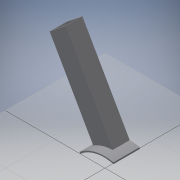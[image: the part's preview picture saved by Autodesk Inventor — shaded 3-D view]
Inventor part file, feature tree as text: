
AUTODESK INVENTOR PART (.ipt)
format: ipt  version: 2019 (Build 230136000, 136)  size: 164,352 bytes
history: native  units: mm
features: other x5, extrude x4, sketch x4, reference x4, projected_geometry x2
ambient origin geometry x8: Origin, YZ Plane, XZ Plane, XY Plane, X Axis, Y Axis, Z Axis, Center Point
bodies: Body1 (feature_tree)
feature tree (19):
  other  "Твердое тело1"
  extrude  "Выдавливание1"  Depth=3.0mm
  extrude  "Выдавливание2"  Depth=3.0mm
  extrude  "Выдавливание3"  Depth=19.0mm TaperAngle=0.0deg
  extrude  "Выдавливание4"  TaperAngle=180.0deg  [1 undecoded]
  sketch  "Эскиз1"
  reference  "Ссылка1"
  reference  "Ссылка2"
  reference  "Ссылка3"
  sketch  "Эскиз3"
  projected_geometry  "Спроецированная петля1"
  reference  "Ссылка8"
  sketch  "Эскиз4"
  projected_geometry  "Спроецированная петля2"
  sketch  "Эскиз5"
  parser-record x1  (decoder bookkeeping rows leaked as tree rows — omitted from the tree; the rows remain in map.json)
  other  "kowsh.iam"
  other  "mot37:1"
  other  "Stenka:1"
note: 1 required parameter value undecoded (feature->parameter linkage not recoverable at this tier; creation-order binding heuristic only, values carry confidence <= 0.55)
note: 1 file-system path scrubbed to <path> (originals preserved in map.json)
